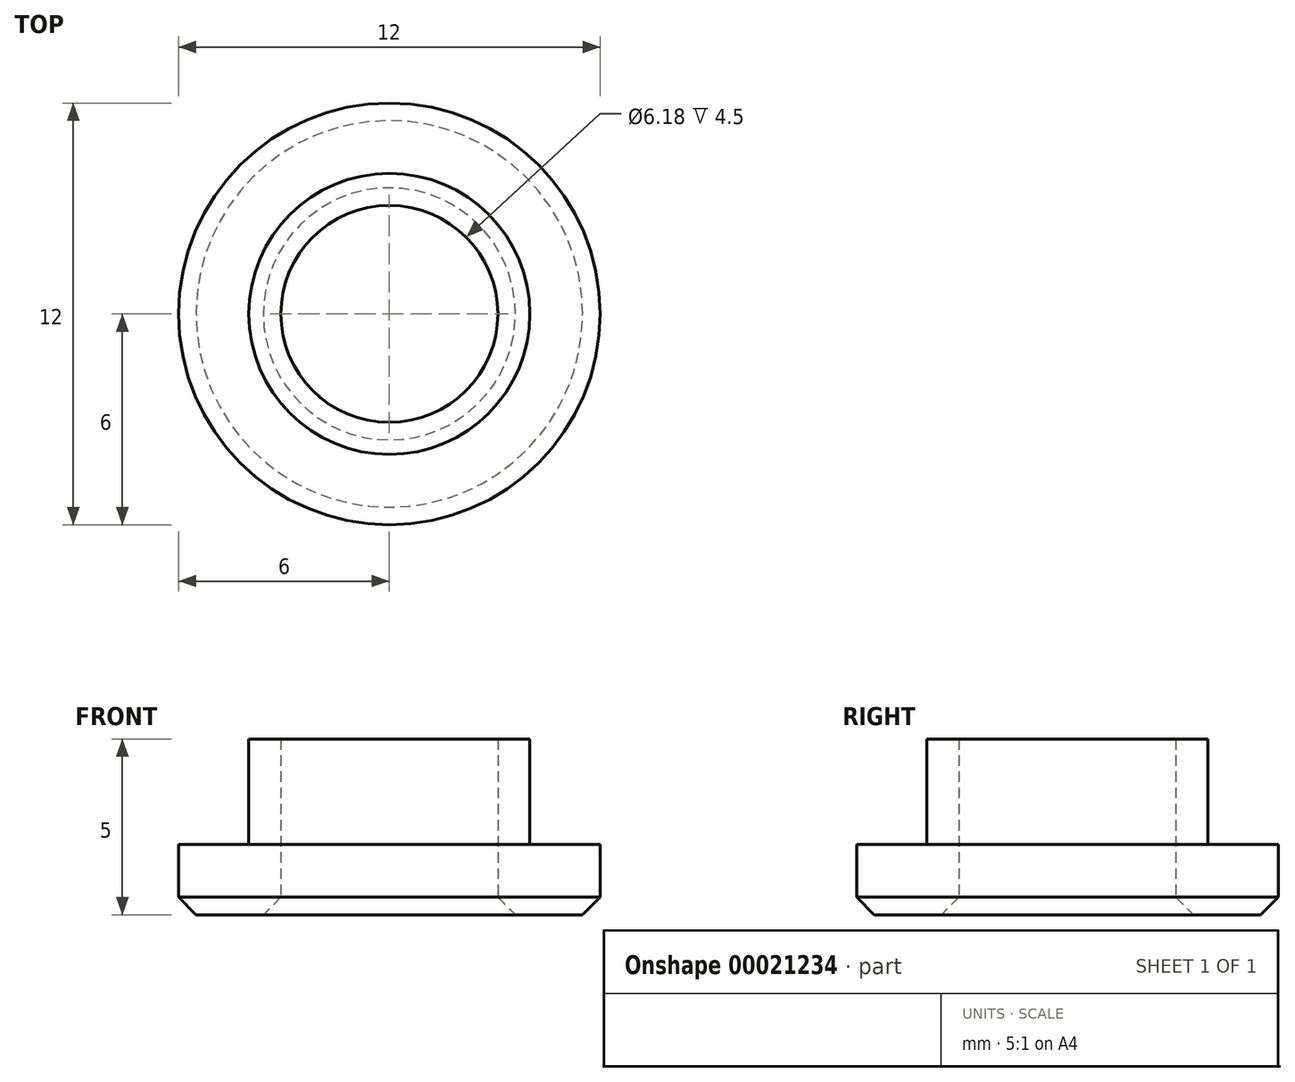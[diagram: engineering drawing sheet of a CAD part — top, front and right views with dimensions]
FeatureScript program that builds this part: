
annotation { "Feature Type Name" : "Feature", "Feature Type Description" : "" }
export const myFeature = defineFeature(function(context is Context, id is Id, definition is map)
    precondition{}
    {
        {
            var Q0;
            Q0=qCreatedBy(makeId("Top.planeOp"),FACE);
            var sketch = newSketch(context, id + "F0", { "sketchPlane" : qUnion([Q0])});
            skCircle(sketch, "E0", {"center": v(0, 0) * mm, "radius": 6 * mm});
            skCircle(sketch, "E1", {"center": v(0, 0) * mm, "radius": 4 * mm});
            skCircle(sketch, "E2", {"center": v(0, 0) * mm, "radius": 3.09 * mm});
            skSolve(sketch);
        }
        {
            var Q0;
            Q0=makeQuery(id+"F0.imprint","IMPRINT",FACE,{"disambiguationData":[TD([[makeQuery(id+"F0.imprint","IMPRINT",EDGE,{"derivedFrom":sQuery(id+"F0.wireOp",EDGE,"E0")}),1.0]])]});
            extrude(context, id + "F1", {"entities" : qUnion([Q0]), "depth" : 2 * mm});
        }
        {
            var Q0;
            Q0=makeQuery(id+"F0.imprint","IMPRINT",FACE,{"disambiguationData":[TD([[makeQuery(id+"F0.imprint","IMPRINT",EDGE,{"derivedFrom":sQuery(id+"F0.wireOp",EDGE,"E1")}),1.0]])]});
            extrude(context, id + "F2", {"entities" : qUnion([Q0]), "operationType" : NewBodyOperationType.ADD, "depth" : 5 * mm});
        }
        {
            var Q0;
            Q0=makeQuery(id+"F2.opExtrude","CAP_EDGE",EDGE,{"disambiguationData":[OSD([sQuery(id+"F0.wireOp",EDGE,"E2")])],"isStart":true});
            var Q1;
            Q1=makeQuery(id+"F1.opExtrude","CAP_EDGE",EDGE,{"disambiguationData":[OSD([sQuery(id+"F0.wireOp",EDGE,"E0")])],"isStart":true});
            chamfer(context, id + "F3", {"entities" : qUnion([Q0, Q1]), "width" : 0.5 * mm, "tangentPropagation" : true});
        }
    });
